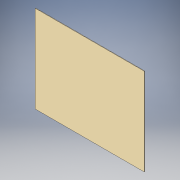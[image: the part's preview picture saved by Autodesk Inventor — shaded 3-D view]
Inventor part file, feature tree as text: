
AUTODESK INVENTOR PART (.ipt)
format: ipt  version: 2019 (Build 230136000, 136)  size: 89,088 bytes
history: native  units: mm
features: extrude x1, sketch x1
ambient origin geometry x8: Origin, YZ Plane, XZ Plane, XY Plane, X Axis, Y Axis, Z Axis, Center Point
bodies: Solid1 (feature_tree)
feature tree (2):
  extrude  "Extrusion1"  Depth=1016.0mm
  sketch  "Sketch1"  dims[d0=4.7625mm d1=0.0mm d2=1016.0mm d3=812.8mm]
